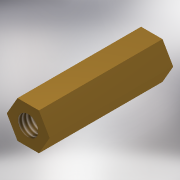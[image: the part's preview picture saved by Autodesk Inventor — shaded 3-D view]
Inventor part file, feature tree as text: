
AUTODESK INVENTOR PART (.ipt)
format: ipt  version: 2018 (Build 220112000, 112)  size: 110,080 bytes
history: native  units: mm
features: sketch x2, extrude x1, hole x1
ambient origin geometry x8: Origin, YZ Plane, XZ Plane, XY Plane, X Axis, Y Axis, Z Axis, Center Point
bodies: Solid1 (feature_tree)
feature tree (4):
  extrude  "Extrusion1"  Depth=20.0mm TaperAngle=0.0deg
  hole  "Hole1"  [1 undecoded]
  sketch  "Sketch1"  dims[d0=3.0mm d1=20.0mm d2=0.0mm]
  sketch  "Sketch2"  dims[d3=3.242mm d4=8.0mm d5=4.0mm d6=2.0mm d7=90.0deg d8=8.0mm d9=20.594885mm]
note: 1 required parameter value undecoded (feature->parameter linkage not recoverable at this tier; creation-order binding heuristic only, values carry confidence <= 0.55)
